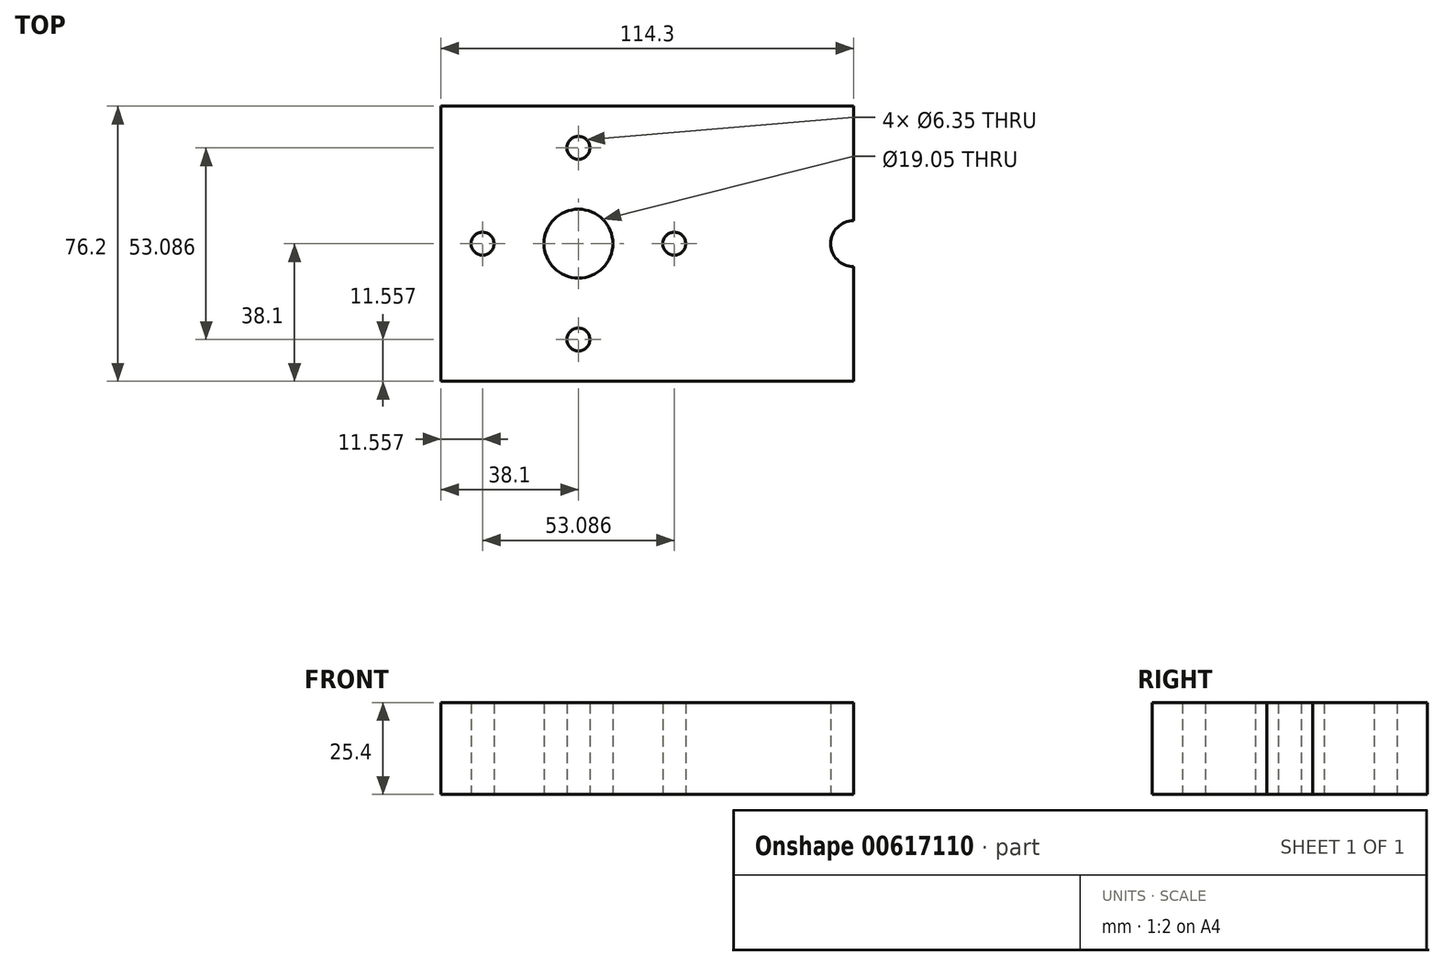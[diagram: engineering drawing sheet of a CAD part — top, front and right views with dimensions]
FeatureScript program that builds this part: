
annotation { "Feature Type Name" : "Feature", "Feature Type Description" : "" }
export const myFeature = defineFeature(function(context is Context, id is Id, definition is map)
    precondition{}
    {
        {
            var Q0;
            Q0=qCreatedBy(makeId("Top.planeOp"),FACE);
            var sketch = newSketch(context, id + "F0", { "sketchPlane" : qUnion([Q0])});
            skLineSegment(sketch, "E0.bottom", {"start": v(-114.3, 38.1) * mm, "end": v(0, 38.1) * mm});
            skLineSegment(sketch, "E0.top", {"start": v(-114.3, -38.1) * mm, "end": v(0, -38.1) * mm});
            skLineSegment(sketch, "E0.left", {"start": v(-114.3, 38.1) * mm, "end": v(-114.3, -38.1) * mm});
            skLineSegment(sketch, "E0.right", {"start": v(0, 38.1) * mm, "end": v(0, 6.35) * mm});
            skLineSegment(sketch, "E1", {"start": v(0, -6.35) * mm, "end": v(0, -38.1) * mm});
            skArc(sketch, "E2", {"start": v(0, 6.35) * mm, "mid": v(-6.35, 0) * mm, "end": v(0, -6.35) * mm});
            skCircle(sketch, "E3", {"center": v(-76.2, 0) * mm, "radius": 9.53 * mm});
            skCircle(sketch, "E4", {"center": v(-76.2, 26.54) * mm, "radius": 3.18 * mm});
            skCircle(sketch, "E5", {"center": v(-102.74, 0) * mm, "radius": 3.18 * mm});
            skCircle(sketch, "E6", {"center": v(-49.66, 0) * mm, "radius": 3.18 * mm});
            skCircle(sketch, "E7", {"center": v(-76.2, -26.54) * mm, "radius": 3.18 * mm});
            skLineSegment(sketch, "E8", {"start": v(-76.2, 38.1) * mm, "end": v(-76.2, -38.1) * mm, "construction": true});
            skSolve(sketch);
        }
        {
            var Q0;
            Q0 = qSketchRegion(id + "F0", true);
            extrude(context, id + "F1", {"entities" : qUnion([Q0]), "depth" : 25.4 * mm, "offsetDistance" : 25.4 * mm});
        }
    });
